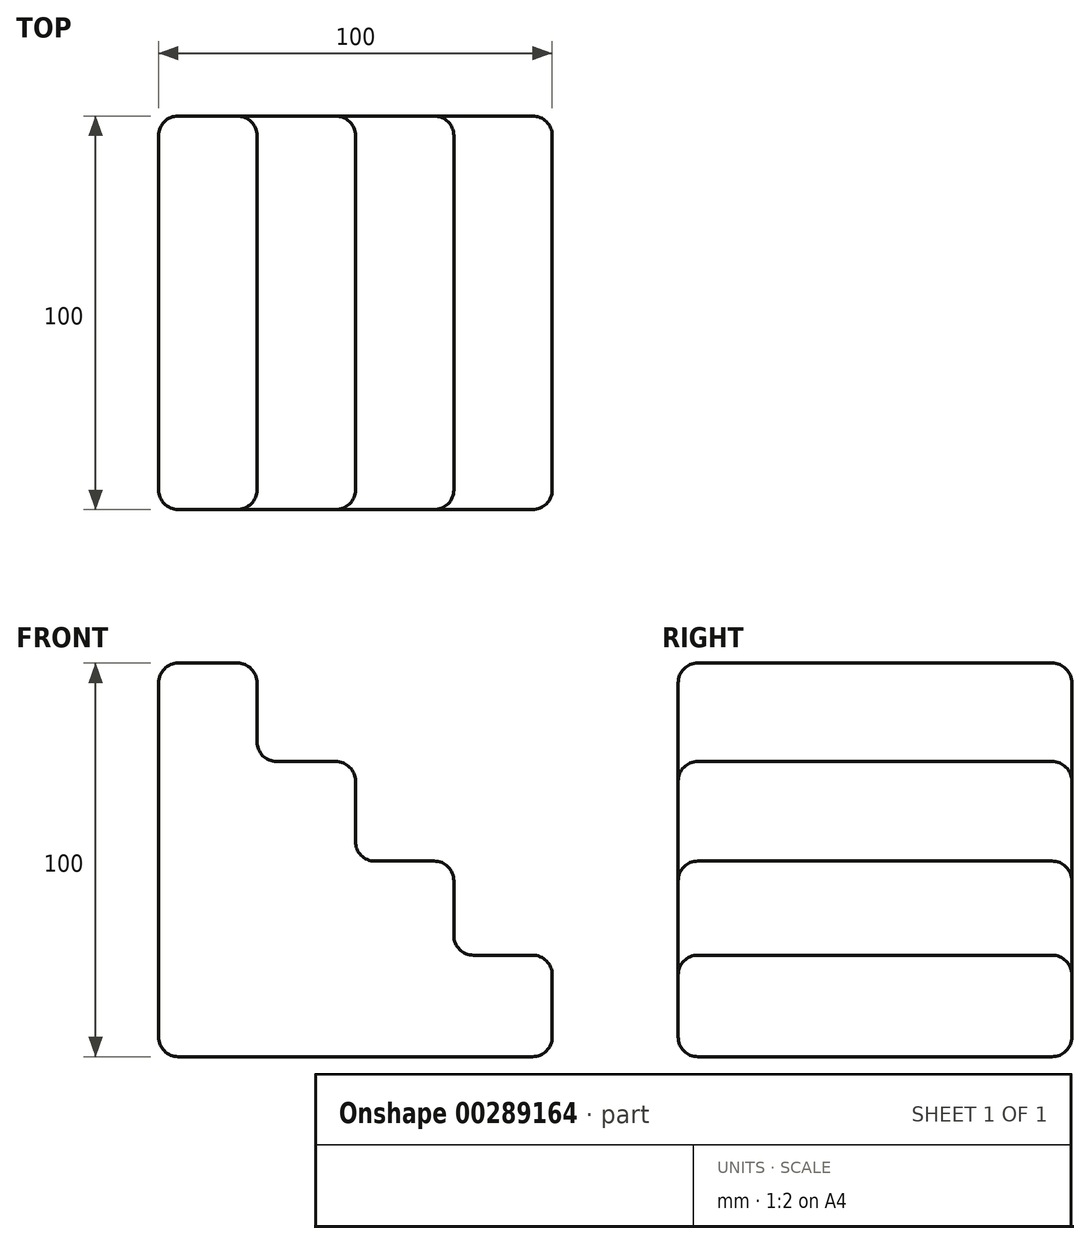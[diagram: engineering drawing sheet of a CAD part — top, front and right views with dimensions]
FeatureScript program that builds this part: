
annotation { "Feature Type Name" : "Feature", "Feature Type Description" : "" }
export const myFeature = defineFeature(function(context is Context, id is Id, definition is map)
    precondition{}
    {
        {
            var Q0;
            Q0=qCreatedBy(makeId("Top.planeOp"),FACE);
            var sketch = newSketch(context, id + "F0", { "sketchPlane" : qUnion([Q0])});
            skLineSegment(sketch, "E0.bottom", {"start": v(0, 0) * mm, "end": v(100, 0) * mm});
            skLineSegment(sketch, "E0.top", {"start": v(0, 100) * mm, "end": v(100, 100) * mm});
            skLineSegment(sketch, "E0.left", {"start": v(0, 0) * mm, "end": v(0, 100) * mm});
            skLineSegment(sketch, "E0.right", {"start": v(100, 0) * mm, "end": v(100, 100) * mm});
            skSolve(sketch);
        }
        {
            var Q0;
            Q0=makeQuery(id+"F0.imprint","IMPRINT",FACE,{"disambiguationData":[TD([[makeQuery(id+"F0.imprint","IMPRINT",EDGE,{"derivedFrom":sQuery(id+"F0.wireOp",EDGE,"E0.bottom")}),1.0]])]});
            extrude(context, id + "F1", {"entities" : qUnion([Q0]), "depth" : 100 * mm});
        }
        {
            var Q0;
            Q0=makeQuery(id+"F1.opExtrude","SWEPT_FACE",FACE,{"disambiguationData":[OSD([sQuery(id+"F0.wireOp",EDGE,"E0.bottom")])]});
            var sketch = newSketch(context, id + "F2", { "sketchPlane" : qUnion([Q0])});
            skLineSegment(sketch, "E1", {"start": v(25, 100) * mm, "end": v(25, 75) * mm});
            skLineSegment(sketch, "E2", {"start": v(25, 75) * mm, "end": v(50, 75) * mm});
            skLineSegment(sketch, "E3", {"start": v(50, 75) * mm, "end": v(50, 49.7) * mm});
            skLineSegment(sketch, "E4", {"start": v(50, 49.7) * mm, "end": v(75, 49.7) * mm});
            skLineSegment(sketch, "E5", {"start": v(75, 49.7) * mm, "end": v(75, 25.77) * mm});
            skLineSegment(sketch, "E6", {"start": v(75, 25.77) * mm, "end": v(100, 25.77) * mm});
            skSolve(sketch);
        }
        {
            var Q0;
            {var subQ0=sQuery(id+"F2.wireOp",EDGE,"E1");Q0=makeQuery(id+"F2.imprint","IMPRINT",FACE,{"disambiguationData":[TD([[makeQuery(id+"F2.imprint","IMPRINT",EDGE,{"derivedFrom":subQ0}),1.0]])]});}
            extrude(context, id + "F3", {"entities" : qUnion([Q0]), "operationType" : NewBodyOperationType.REMOVE, "oppositeDirection" : true, "depth" : 107.7 * mm});
        }
        {
            var Q0;
            Q0=makeQuery(id+"F3.boolean.opBoolean","COPY",FACE,{"derivedFrom":makeQuery(id+"F3.opExtrude","SWEPT_FACE",FACE,{"disambiguationData":[OSD([sQuery(id+"F2.wireOp",EDGE,"E1")])]})});
            fillet(context, id + "F4", {"entities" : qUnion([Q0]), "radius" : 5 * mm, "tangentPropagation" : true, "allowEdgeOverflow" : false});
        }
        {
            var Q0;
            Q0=makeQuery(id+"F1.opExtrude","CAP_FACE",FACE,{"disambiguationData":[OSD([sQuery(id+"F0.wireOp",EDGE,"E0.bottom"),sQuery(id+"F0.wireOp",EDGE,"E0.top"),sQuery(id+"F0.wireOp",EDGE,"E0.left"),sQuery(id+"F0.wireOp",EDGE,"E0.right")])],"isStart":false});
            var Q1;
            Q1=makeQuery(id+"F3.boolean.opBoolean","COPY",FACE,{"derivedFrom":makeQuery(id+"F3.opExtrude","SWEPT_FACE",FACE,{"disambiguationData":[OSD([sQuery(id+"F2.wireOp",EDGE,"E3")])]})});
            var Q2;
            Q2=makeQuery(id+"F3.boolean.opBoolean","COPY",FACE,{"derivedFrom":makeQuery(id+"F3.opExtrude","SWEPT_FACE",FACE,{"disambiguationData":[OSD([sQuery(id+"F2.wireOp",EDGE,"E5")])]})});
            var Q3;
            Q3=makeQuery(id+"F1.opExtrude","SWEPT_FACE",FACE,{"disambiguationData":[OSD([sQuery(id+"F0.wireOp",EDGE,"E0.right")])]});
            var Q4;
            Q4=makeQuery(id+"F1.opExtrude","SWEPT_FACE",FACE,{"disambiguationData":[OSD([sQuery(id+"F0.wireOp",EDGE,"E0.bottom")])]});
            var Q5;
            Q5=makeQuery(id+"F1.opExtrude","SWEPT_FACE",FACE,{"disambiguationData":[OSD([sQuery(id+"F0.wireOp",EDGE,"E0.top")])]});
            var Q6;
            Q6=makeQuery(id+"F1.opExtrude","SWEPT_FACE",FACE,{"disambiguationData":[OSD([sQuery(id+"F0.wireOp",EDGE,"E0.left")])]});
            fillet(context, id + "F5", {"entities" : qUnion([Q0, Q1, Q2, Q3, Q4, Q5, Q6]), "radius" : 5 * mm, "tangentPropagation" : true, "allowEdgeOverflow" : false});
        }
    });
